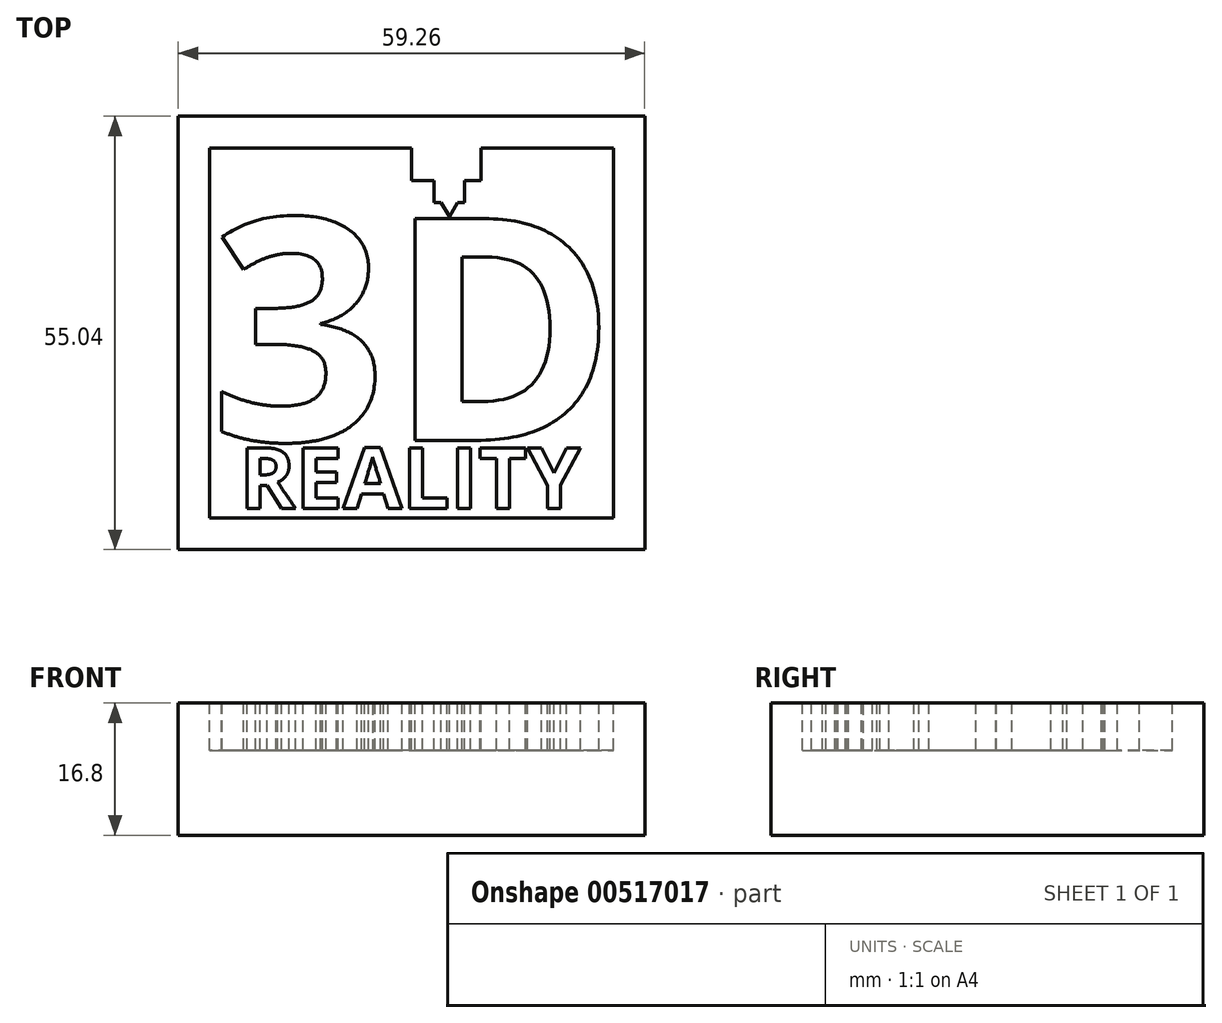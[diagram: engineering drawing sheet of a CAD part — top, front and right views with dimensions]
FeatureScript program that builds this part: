
annotation { "Feature Type Name" : "Feature", "Feature Type Description" : "" }
export const myFeature = defineFeature(function(context is Context, id is Id, definition is map)
    precondition{}
    {
        {
            var Q0;
            Q0=qCreatedBy(makeId("Top.planeOp"),FACE);
            var sketch = newSketch(context, id + "F0", { "sketchPlane" : qUnion([Q0])});
            skLineSegment(sketch, "E0.bottom", {"start": v(-12.44, -15.22) * mm, "end": v(17.19, -15.22) * mm});
            skLineSegment(sketch, "E0.top", {"start": v(-12.44, 24.78) * mm, "end": v(17.19, 24.78) * mm});
            skLineSegment(sketch, "E0.left", {"start": v(-12.44, -15.22) * mm, "end": v(-12.44, 24.78) * mm});
            skLineSegment(sketch, "E0.right", {"start": v(17.19, -15.22) * mm, "end": v(17.19, 24.78) * mm});
            skLineSegment(sketch, "E1", {"start": v(-12.44, 12.3) * mm, "end": v(17.19, 12.3) * mm});
            skLineSegment(sketch, "E2", {"start": v(-12.44, 12.3) * mm, "end": v(-12.44, -15.22) * mm});
            skSolve(sketch);
        }
        {
            var Q0;
            {var subQ0=sQuery(id+"F0.wireOp",EDGE,"E0.bottom");Q0=makeQuery(id+"F0.imprint","IMPRINT",FACE,{"disambiguationData":[TD([[makeQuery(id+"F0.imprint","IMPRINT",EDGE,{"derivedFrom":subQ0}),1.0]])]});}
            extrude(context, id + "F1", {"entities" : qUnion([Q0]), "depth" : 8.4 * mm, "offsetDistance" : 25 * mm});
        }
        {
            var Q0;
            Q0=makeQuery(id+"F1.opExtrude","CAP_FACE",FACE,{"disambiguationData":[OSD([sQuery(id+"F0.wireOp",EDGE,"E0.bottom"),sQuery(id+"F0.wireOp",EDGE,"E0.top"),sQuery(id+"F0.wireOp",EDGE,"E0.left"),sQuery(id+"F0.wireOp",EDGE,"E0.right")])],"isStart":false});
            var sketch = newSketch(context, id + "F2", { "sketchPlane" : qUnion([Q0])});
            skLineSegment(sketch, "E3", {"start": v(-10.44, -13.22) * mm, "end": v(-10.44, 10.28) * mm});
            skLineSegment(sketch, "E4", {"start": v(-10.44, -13.22) * mm, "end": v(15.19, -13.22) * mm});
            skLineSegment(sketch, "E5", {"start": v(15.19, -13.22) * mm, "end": v(15.19, 9.26) * mm});
            skLineSegment(sketch, "E6", {"start": v(15.19, 10.28) * mm, "end": v(15.19, 10.28) * mm});
            skLineSegment(sketch, "E7", {"start": v(15.19, 10.28) * mm, "end": v(-10.44, 10.28) * mm});
            skLineSegment(sketch, "E8", {"start": v(-10.44, 10.28) * mm, "end": v(-10.44, 10.28) * mm});
            skPoint(sketch, "E9", {"position": v(15.19, -1.98) * mm});
            skPoint(sketch, "E10", {"position": v(2.37, 10.28) * mm});
            skText(sketch, "E11", { "text": "REALITY", "fontName": "OpenSans-Bold.ttf"});
            skLineSegment(sketch, "E12", {"start": v(13.9, -8.73) * mm, "end": v(13.9, -12.62) * mm});
            skLineSegment(sketch, "E13", {"start": v(13.45, -8.28) * mm, "end": v(3.09, -8.28) * mm});
            skLineSegment(sketch, "E14", {"start": v(3.09, -8.28) * mm, "end": v(-8.55, -8.28) * mm});
            skLineSegment(sketch, "E15", {"start": v(-9, -8.73) * mm, "end": v(-9, -12.62) * mm});
            skLineSegment(sketch, "E16", {"start": v(-8.55, -13.07) * mm, "end": v(13.45, -13.07) * mm});
            skArc(sketch, "E17", {"start": v(13.9, -8.73) * mm, "mid": v(13.76, -8.41) * mm, "end": v(13.45, -8.28) * mm});
            skArc(sketch, "E18", {"start": v(-8.55, -8.28) * mm, "mid": v(-8.87, -8.41) * mm, "end": v(-9, -8.73) * mm});
            skLineSegment(sketch, "E19", {"start": v(-8.55, -8.73) * mm, "end": v(13.45, -8.73) * mm});
            skLineSegment(sketch, "E20", {"start": v(13.45, -12.62) * mm, "end": v(-8.55, -12.62) * mm});
            skLineSegment(sketch, "E21", {"start": v(-8.55, -8.73) * mm, "end": v(-8.55, -12.62) * mm});
            skText(sketch, "E22", { "text": "3D", "fontName": "OpenSans-Bold.ttf"});
            skArc(sketch, "E23", {"start": v(-9, -12.62) * mm, "mid": v(-8.87, -12.93) * mm, "end": v(-8.55, -13.07) * mm});
            skArc(sketch, "E24", {"start": v(13.45, -13.07) * mm, "mid": v(13.76, -12.93) * mm, "end": v(13.9, -12.62) * mm});
            skLineSegment(sketch, "E25", {"start": v(13.45, -8.73) * mm, "end": v(13.45, -12.62) * mm});
            skLineSegment(sketch, "E26.bottom", {"start": v(2.37, 10.28) * mm, "end": v(6.79, 10.28) * mm});
            skLineSegment(sketch, "E26.top", {"start": v(2.37, 8.21) * mm, "end": v(6.79, 8.21) * mm});
            skLineSegment(sketch, "E26.left", {"start": v(2.37, 10.28) * mm, "end": v(2.37, 8.21) * mm});
            skLineSegment(sketch, "E26.right", {"start": v(6.79, 10.28) * mm, "end": v(6.79, 8.21) * mm});
            skLineSegment(sketch, "E27.bottom", {"start": v(3.82, 8.21) * mm, "end": v(5.74, 8.21) * mm});
            skLineSegment(sketch, "E27.top", {"start": v(3.82, 6.82) * mm, "end": v(5.74, 6.82) * mm});
            skLineSegment(sketch, "E27.left", {"start": v(3.82, 8.21) * mm, "end": v(3.82, 6.82) * mm});
            skLineSegment(sketch, "E27.right", {"start": v(5.74, 8.21) * mm, "end": v(5.74, 6.82) * mm});
            skLineSegment(sketch, "E28", {"start": v(4.78, 5.93) * mm, "end": v(4.25, 6.82) * mm});
            skPoint(sketch, "E28.startSnap0", {"position": v(4.78, 6.82) * mm});
            skLineSegment(sketch, "E29", {"start": v(4.78, 5.93) * mm, "end": v(5.29, 6.82) * mm});
            skLineSegment(sketch, "E30", {"start": v(15.19, 9.26) * mm, "end": v(15.19, 10.28) * mm});
            const initialGuessF2  = {"E11": [-0.00855, -0.01262, 1, 0, 0.00389], "E22": [-0.01044, -0.00828, 1, 0, 0.0142]};
            skSetInitialGuess(sketch, initialGuessF2);
            skSolve(sketch);
        }
        {
            var Q0;
            {var subQ14=sQuery(id+"F2.wireOp",EDGE,"E4");Q0=makeQuery(id+"F2.imprint","IMPRINT",FACE,{"disambiguationData":[TD([[makeQuery(id+"F2.imprint","IMPRINT",EDGE,{"derivedFrom":subQ14}),1.0]])]});}
            var Q1;
            Q1=makeQuery(id+"F2.imprint","IMPRINT",FACE,{"disambiguationData":[TD([[makeQuery(id+"F2.imprint","IMPRINT",EDGE,{"derivedFrom":sQuery(id+"F2.wireOp",EDGE,"E22.sketch_text.stroke-34")}),1.0]])]});
            var Q2;
            {var subQ7=sQuery(id+"F2.wireOp",EDGE,"E11.sketch_text.stroke-9");Q2=makeQuery(id+"F2.imprint","IMPRINT",FACE,{"disambiguationData":[TD([[makeQuery(id+"F2.imprint","IMPRINT",EDGE,{"derivedFrom":subQ7}),1.0]])]});}
            var Q3;
            {var subQ0=sQuery(id+"F2.wireOp",EDGE,"E11.sketch_text.stroke-31");Q3=makeQuery(id+"F2.imprint","IMPRINT",FACE,{"disambiguationData":[TD([[makeQuery(id+"F2.imprint","IMPRINT",EDGE,{"derivedFrom":subQ0}),1.0]])]});}
            var Q4;
            Q4=makeQuery(id+"F2.imprint","IMPRINT",FACE,{"disambiguationData":[TD([[makeQuery(id+"F2.imprint","IMPRINT",EDGE,{"derivedFrom":sQuery(id+"F2.wireOp",EDGE,"E11.sketch_text.stroke-39")}),1.0]])]});
            var Q5;
            Q5=makeQuery(id+"F2.imprint","IMPRINT",FACE,{"disambiguationData":[TD([[makeQuery(id+"F2.imprint","IMPRINT",EDGE,{"derivedFrom":sQuery(id+"F2.wireOp",EDGE,"E11.sketch_text.stroke-0")}),1.0]])]});
            var Q6;
            {var subQ0=sQuery(id+"F2.wireOp",EDGE,"E11.sketch_text.stroke-7");Q6=makeQuery(id+"F2.imprint","IMPRINT",FACE,{"disambiguationData":[TD([[makeQuery(id+"F2.imprint","IMPRINT",EDGE,{"derivedFrom":subQ0}),1.0]])]});}
            var Q7;
            Q7=makeQuery(id+"F2.imprint","IMPRINT",FACE,{"disambiguationData":[TD([[makeQuery(id+"F2.imprint","IMPRINT",EDGE,{"derivedFrom":sQuery(id+"F2.wireOp",EDGE,"yndPzmaS-FrQS-0oLp-HTLf-hFb25hjCLlXs")}),1.0]])]});
            var Q8;
            {var subQ1=sQuery(id+"F2.wireOp",EDGE,"miOvBIj9-mftL-q9TI-mgcK-NAn9a5hrD1wx");Q8=makeQuery(id+"F2.imprint","IMPRINT",FACE,{"disambiguationData":[TD([[makeQuery(id+"F2.imprint","IMPRINT",EDGE,{"derivedFrom":subQ1}),1.0]])]});}
            extrude(context, id + "F3", {"entities" : qUnion([Q0, Q1, Q2, Q3, Q4, Q5, Q6, Q7, Q8]), "operationType" : NewBodyOperationType.REMOVE, "oppositeDirection" : true, "depth" : 3 * mm, "offsetDistance" : 25 * mm});
        }
        {
            var Q0;
            Q0=makeQuery(id+"F1.opExtrude","SWEPT_BODY",BODY,{"disambiguationData":[OSD([sQuery(id+"F0.wireOp",EDGE,"E0.bottom"),sQuery(id+"F0.wireOp",EDGE,"E0.right"),sQuery(id+"F0.wireOp",EDGE,"E1"),sQuery(id+"F0.wireOp",EDGE,"E2")])]});
            var Q1;
            Q1=makeQuery(id+"F1.opExtrude","CAP_VERTEX",VERTEX,{"disambiguationData":[OSD([sQuery(id+"F0.wireOp",EDGE,"E0.bottom"),sQuery(id+"F0.wireOp",EDGE,"E2")])],"isStart":true});
            transform(context, id + "F4", {"entities" : qUnion([Q0]), "transformType" : TransformType.SCALE_UNIFORMLY, "scale" : 2, "scalePoint" : qUnion([Q1]), "makeCopy" : false});
        }
    });
